# Revit family: All-Lite ECV-345
name_source: partatom
category: Mechanical Equipment
units: mm (PartAtom-declared; Revit-internal decimal feet)

## family parameters
Cut with Voids When Loaded = No
Host = Face
Part Type = Normal
Room Calculation Point = No
Round Connector Dimension = Use Diameter
Shared = No

## types (2) — shared parameters
Air Volume Delivered = 9375 cfm
Assembly Code = B3020300
Blades = .06'' thick vertical chevron style.
Default Elevation = 0"
Depth = 6"
Description = The ECV-345 louver is engineered and tested to withstand
extreme loads, debris impact, and cyclic fatigue associated
with the severe weather effects of hurricanes. The design
uses closely-spaced blades and a frame with built-in gutter
and downspouts to achieve maximum water infiltration
resistance for minimal louver depth. The ECV-345 is AMCA
540 and 550 listed, making it ideally suited for use in
hurricane-prone and windborne debris regions as per the
International Building Code.
Design Load = 100 psf
Frame = 3'' deep x 0.075'' thick channel.
Free Area (48" x 48") = 7.5 ft² 46.9%
Free Area Velocity = 1250 fpm
Manufacturer = All-Lite
Material = Mill finish 6063-T5 extruded aluminum.
Maximum Height = 96"
Maximum Width = 60"
Minimum Height = 12"
Minimum Width = 12"
Model = ECV-345
Modeled By = Commense Studio
Mullion = Visible
Pressure Loss = .19 in. wg
Screen = 1/2'' x 0.063'' expanded and flattened aluminum.
Velocity @ .15 in.wg. Pressure Loss = 1106 fpm

## per-type parameters (varying)
| type | Array Control 1 | Array Control 2 | Blade Height | Height | Height Control | Product URL | URL | Width | Width Control |
| 60" x 120" | 146 | 146 | 118 7/32" | 120" | 120" | https://www.alllite.com | https://www.alllite.com | 60" | 60" |
| 36" x 48" | 50 | 50 | 46 7/32" | 48" | 48" |  | https://www.pottorff.com | 36" | 36" |

## geometry (parser evidence)
native form markers: Blend x8, Sweep x10
no freeform markers — native parametric forms only
